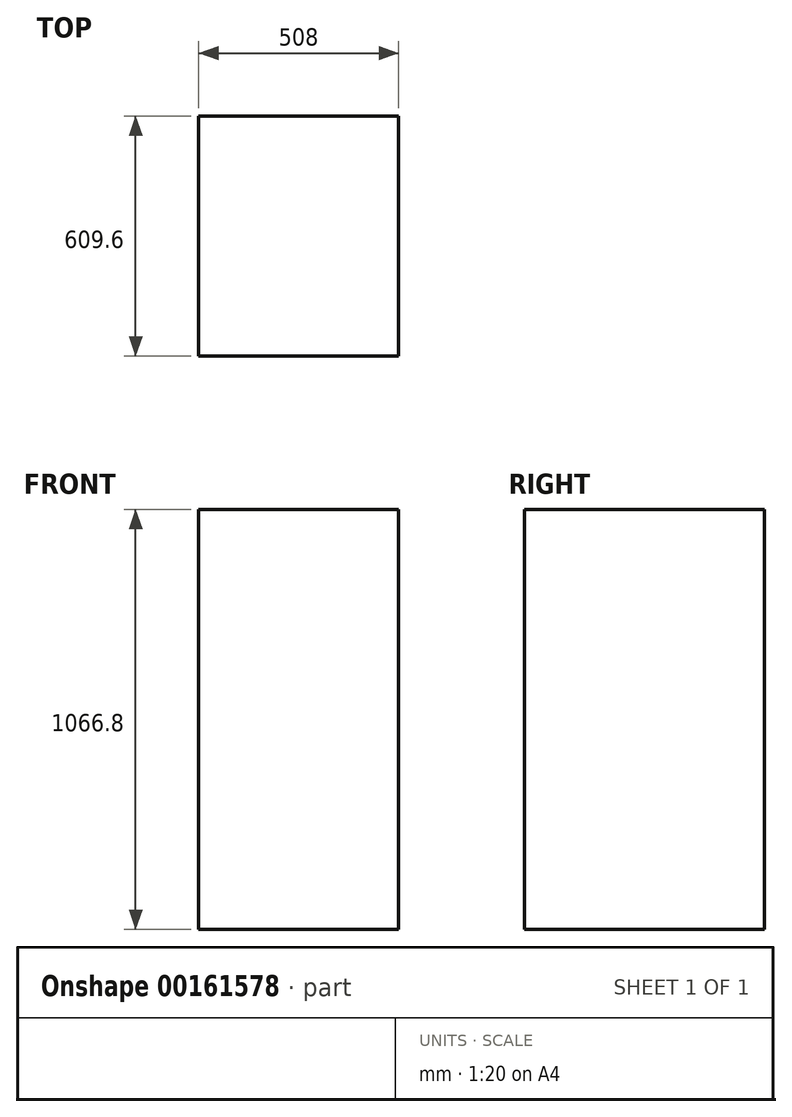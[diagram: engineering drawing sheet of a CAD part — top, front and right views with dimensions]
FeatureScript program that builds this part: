
annotation { "Feature Type Name" : "Feature", "Feature Type Description" : "" }
export const myFeature = defineFeature(function(context is Context, id is Id, definition is map)
    precondition{}
    {
        {
            var Q0;
            Q0=qCreatedBy(makeId("Top.planeOp"),FACE);
            var sketch = newSketch(context, id + "F0", { "sketchPlane" : qUnion([Q0])});
            skLineSegment(sketch, "E0.bottom", {"start": v(254, 304.8) * mm, "end": v(-254, 304.8) * mm});
            skLineSegment(sketch, "E0.top", {"start": v(254, -304.8) * mm, "end": v(-254, -304.8) * mm});
            skLineSegment(sketch, "E0.left", {"start": v(254, 304.8) * mm, "end": v(254, -304.8) * mm});
            skLineSegment(sketch, "E0.right", {"start": v(-254, 304.8) * mm, "end": v(-254, -304.8) * mm});
            skPoint(sketch, "E0.middle", {"position": v(0, 0) * mm});
            skSolve(sketch);
        }
        {
            var Q0;
            Q0 = qSketchRegion(id + "F0", true);
            extrude(context, id + "F1", {"entities" : qUnion([Q0]), "depth" : 1066.8 * mm});
        }
    });
